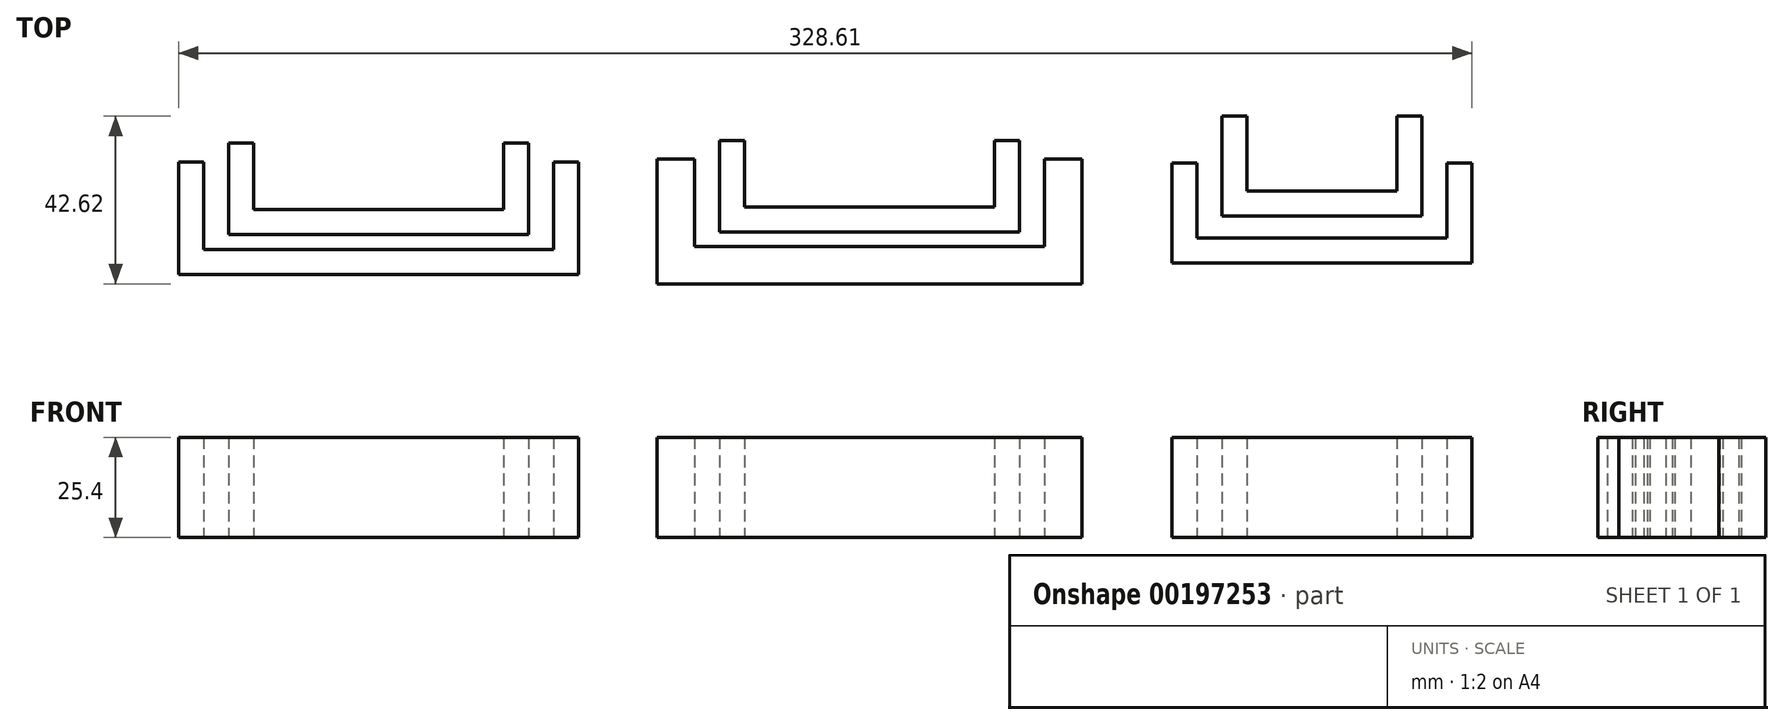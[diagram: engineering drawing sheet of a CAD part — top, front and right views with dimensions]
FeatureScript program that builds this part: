
annotation { "Feature Type Name" : "Feature", "Feature Type Description" : "" }
export const myFeature = defineFeature(function(context is Context, id is Id, definition is map)
    precondition{}
    {
        {
            var Q0;
            Q0=qCreatedBy(makeId("Top.planeOp"),FACE);
            var sketch = newSketch(context, id + "F0", { "sketchPlane" : qUnion([Q0])});
            skLineSegment(sketch, "E0", {"start": v(-118.66, -13) * mm, "end": v(-118.66, 15.58) * mm});
            skLineSegment(sketch, "E1", {"start": v(-118.66, 15.58) * mm, "end": v(-112.31, 15.58) * mm});
            skLineSegment(sketch, "E2", {"start": v(-112.31, 15.58) * mm, "end": v(-112.31, -6.65) * mm});
            skLineSegment(sketch, "E3", {"start": v(-112.31, -6.65) * mm, "end": v(-23.41, -6.65) * mm});
            skLineSegment(sketch, "E4", {"start": v(-23.41, -6.65) * mm, "end": v(-23.41, 15.58) * mm});
            skLineSegment(sketch, "E5", {"start": v(-23.41, 15.58) * mm, "end": v(-17.06, 15.58) * mm});
            skLineSegment(sketch, "E6", {"start": v(-17.06, 15.58) * mm, "end": v(-17.06, -13) * mm});
            skLineSegment(sketch, "E7", {"start": v(-17.06, -13) * mm, "end": v(-118.66, -13) * mm});
            skLineSegment(sketch, "E8", {"start": v(-67.86, 16.41) * mm, "end": v(-67.86, -31.16) * mm, "construction": true});
            skPoint(sketch, "E8.startSnap0", {"position": v(-67.86, -6.65) * mm});
            skLineSegment(sketch, "E9", {"start": v(-105.96, 20.34) * mm, "end": v(-105.96, -2.81) * mm});
            skLineSegment(sketch, "E10", {"start": v(-105.96, -2.81) * mm, "end": v(-29.76, -2.81) * mm});
            skLineSegment(sketch, "E11", {"start": v(-29.76, -2.81) * mm, "end": v(-29.76, 20.34) * mm});
            skLineSegment(sketch, "E12", {"start": v(-29.76, 20.34) * mm, "end": v(-36.11, 20.34) * mm});
            skLineSegment(sketch, "E13", {"start": v(-36.11, 20.34) * mm, "end": v(-36.11, 3.54) * mm});
            skLineSegment(sketch, "E14", {"start": v(-36.11, 3.54) * mm, "end": v(-99.61, 3.54) * mm});
            skLineSegment(sketch, "E15", {"start": v(-99.61, 3.54) * mm, "end": v(-99.61, 20.34) * mm});
            skLineSegment(sketch, "E16", {"start": v(-99.61, 20.34) * mm, "end": v(-105.96, 20.34) * mm});
            skSolve(sketch);
        }
        {
            var Q0;
            Q0 = qSketchRegion(id + "F0", true);
            extrude(context, id + "F1", {"entities" : qUnion([Q0]), "depth" : 25.4 * mm});
        }
        {
            var Q0;
            Q0=qCreatedBy(makeId("Top.planeOp"),FACE);
            var sketch = newSketch(context, id + "F2", { "sketchPlane" : qUnion([Q0])});
            skLineSegment(sketch, "E17", {"start": v(2.86, 16.34) * mm, "end": v(2.86, -15.4) * mm});
            skLineSegment(sketch, "E18", {"start": v(2.86, -15.4) * mm, "end": v(110.8, -15.4) * mm});
            skLineSegment(sketch, "E19", {"start": v(110.8, -15.4) * mm, "end": v(110.8, 16.34) * mm});
            skLineSegment(sketch, "E20", {"start": v(110.8, 16.34) * mm, "end": v(101.28, 16.34) * mm});
            skLineSegment(sketch, "E21", {"start": v(101.28, 16.34) * mm, "end": v(101.28, -5.88) * mm});
            skLineSegment(sketch, "E22", {"start": v(101.28, -5.88) * mm, "end": v(12.38, -5.88) * mm});
            skLineSegment(sketch, "E23", {"start": v(12.38, -5.88) * mm, "end": v(12.38, 16.34) * mm});
            skLineSegment(sketch, "E24", {"start": v(12.38, 16.34) * mm, "end": v(2.86, 16.34) * mm});
            skLineSegment(sketch, "E25", {"start": v(18.73, 20.98) * mm, "end": v(18.73, -2.21) * mm});
            skLineSegment(sketch, "E26", {"start": v(18.73, -2.21) * mm, "end": v(94.93, -2.21) * mm});
            skLineSegment(sketch, "E27", {"start": v(94.93, -2.21) * mm, "end": v(94.93, 20.98) * mm});
            skLineSegment(sketch, "E28", {"start": v(94.93, 20.98) * mm, "end": v(88.58, 20.98) * mm});
            skLineSegment(sketch, "E29", {"start": v(88.58, 20.98) * mm, "end": v(88.58, 4.14) * mm});
            skLineSegment(sketch, "E30", {"start": v(88.58, 4.14) * mm, "end": v(25.08, 4.14) * mm});
            skLineSegment(sketch, "E31", {"start": v(25.08, 4.14) * mm, "end": v(25.08, 20.98) * mm});
            skLineSegment(sketch, "E32", {"start": v(25.08, 20.98) * mm, "end": v(18.73, 20.98) * mm});
            skLineSegment(sketch, "E33", {"start": v(56.83, 12) * mm, "end": v(56.83, -25.9) * mm, "construction": true});
            skPoint(sketch, "E33.startSnap0", {"position": v(56.83, 4.14) * mm});
            skSolve(sketch);
        }
        {
            var Q0;
            Q0 = qSketchRegion(id + "F2", true);
            extrude(context, id + "F3", {"entities" : qUnion([Q0]), "depth" : 25.4 * mm});
        }
        {
            var Q0;
            Q0=qCreatedBy(makeId("Top.planeOp"),FACE);
            var sketch = newSketch(context, id + "F4", { "sketchPlane" : qUnion([Q0])});
            skLineSegment(sketch, "E34", {"start": v(133.75, 15.3) * mm, "end": v(133.75, -10.1) * mm});
            skLineSegment(sketch, "E35", {"start": v(133.75, -10.1) * mm, "end": v(209.95, -10.1) * mm});
            skLineSegment(sketch, "E36", {"start": v(209.95, -10.1) * mm, "end": v(209.95, 15.3) * mm});
            skLineSegment(sketch, "E37", {"start": v(209.95, 15.3) * mm, "end": v(203.6, 15.3) * mm});
            skLineSegment(sketch, "E38", {"start": v(203.6, 15.3) * mm, "end": v(203.6, -3.74) * mm});
            skLineSegment(sketch, "E39", {"start": v(203.6, -3.74) * mm, "end": v(140.1, -3.74) * mm});
            skLineSegment(sketch, "E40", {"start": v(140.1, -3.74) * mm, "end": v(140.1, 15.3) * mm});
            skLineSegment(sketch, "E41", {"start": v(140.1, 15.3) * mm, "end": v(133.75, 15.3) * mm});
            skLineSegment(sketch, "E42", {"start": v(171.85, 6.22) * mm, "end": v(171.85, -26.54) * mm, "construction": true});
            skPoint(sketch, "E42.startSnap0", {"position": v(171.85, -3.74) * mm});
            skLineSegment(sketch, "E43", {"start": v(146.45, 27.21) * mm, "end": v(146.45, 1.81) * mm});
            skLineSegment(sketch, "E44", {"start": v(146.45, 1.81) * mm, "end": v(197.25, 1.81) * mm});
            skLineSegment(sketch, "E45", {"start": v(197.25, 1.81) * mm, "end": v(197.25, 27.21) * mm});
            skLineSegment(sketch, "E46", {"start": v(197.25, 27.21) * mm, "end": v(190.9, 27.21) * mm});
            skLineSegment(sketch, "E47", {"start": v(190.9, 27.21) * mm, "end": v(190.9, 8.16) * mm});
            skLineSegment(sketch, "E48", {"start": v(190.9, 8.16) * mm, "end": v(152.8, 8.16) * mm});
            skLineSegment(sketch, "E49", {"start": v(152.8, 8.16) * mm, "end": v(152.8, 27.21) * mm});
            skLineSegment(sketch, "E50", {"start": v(152.8, 27.21) * mm, "end": v(146.45, 27.21) * mm});
            skSolve(sketch);
        }
        {
            var Q0;
            Q0 = qSketchRegion(id + "F4", true);
            extrude(context, id + "F5", {"entities" : qUnion([Q0]), "depth" : 25.4 * mm});
        }
    });
